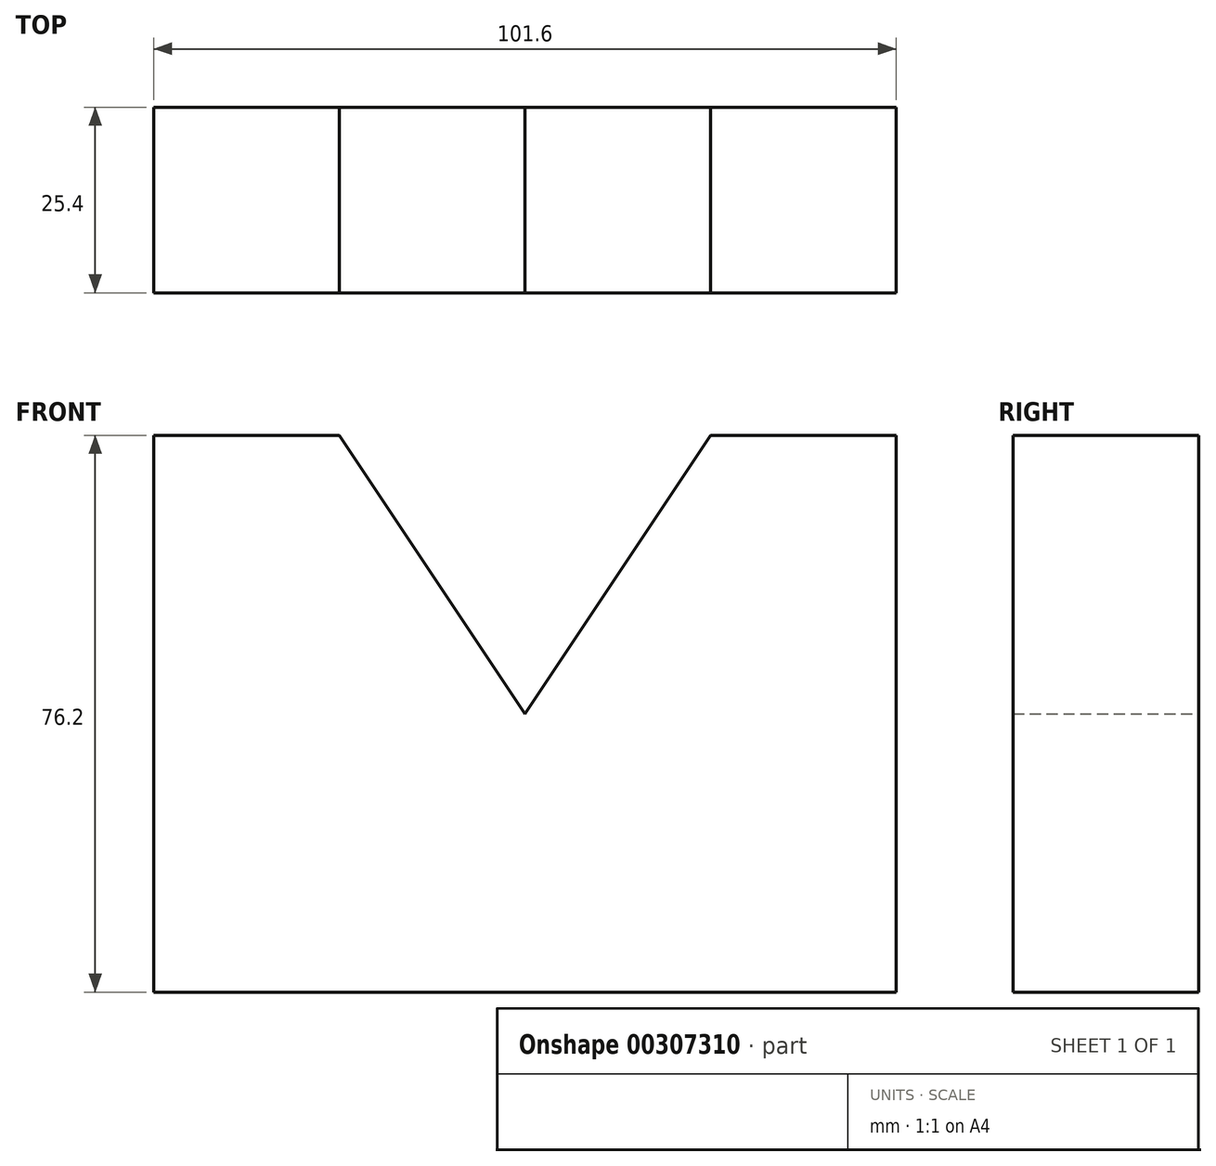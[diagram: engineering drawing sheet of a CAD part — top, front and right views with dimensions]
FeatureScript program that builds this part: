
annotation { "Feature Type Name" : "Feature", "Feature Type Description" : "" }
export const myFeature = defineFeature(function(context is Context, id is Id, definition is map)
    precondition{}
    {
        {
            var Q0;
            Q0=qCreatedBy(makeId("Front.planeOp"),FACE);
            var sketch = newSketch(context, id + "F0", { "sketchPlane" : qUnion([Q0])});
            skLineSegment(sketch, "E0", {"start": v(9.68, 47.91) * mm, "end": v(35.08, 47.91) * mm});
            skLineSegment(sketch, "E1", {"start": v(35.08, 47.91) * mm, "end": v(35.08, -28.29) * mm});
            skLineSegment(sketch, "E2", {"start": v(35.08, -28.29) * mm, "end": v(-66.52, -28.29) * mm});
            skLineSegment(sketch, "E3", {"start": v(-66.52, -28.29) * mm, "end": v(-66.52, 47.91) * mm});
            skLineSegment(sketch, "E4", {"start": v(-66.52, 47.91) * mm, "end": v(-41.12, 47.91) * mm});
            skLineSegment(sketch, "E5", {"start": v(-41.12, 47.91) * mm, "end": v(-15.72, 9.81) * mm});
            skPoint(sketch, "E5.endSnap0", {"position": v(-15.72, -28.29) * mm});
            skLineSegment(sketch, "E6", {"start": v(-15.72, 9.81) * mm, "end": v(9.68, 47.91) * mm});
            skSolve(sketch);
        }
        {
            var Q0;
            Q0=makeQuery(id+"F0.imprint","IMPRINT",FACE,{"disambiguationData":[TD([[makeQuery(id+"F0.imprint","IMPRINT",EDGE,{"derivedFrom":sQuery(id+"F0.wireOp",EDGE,"E0")}),-1.0]])]});
            extrude(context, id + "F1", {"entities" : qUnion([Q0]), "depth" : 25.4 * mm});
        }
    });
